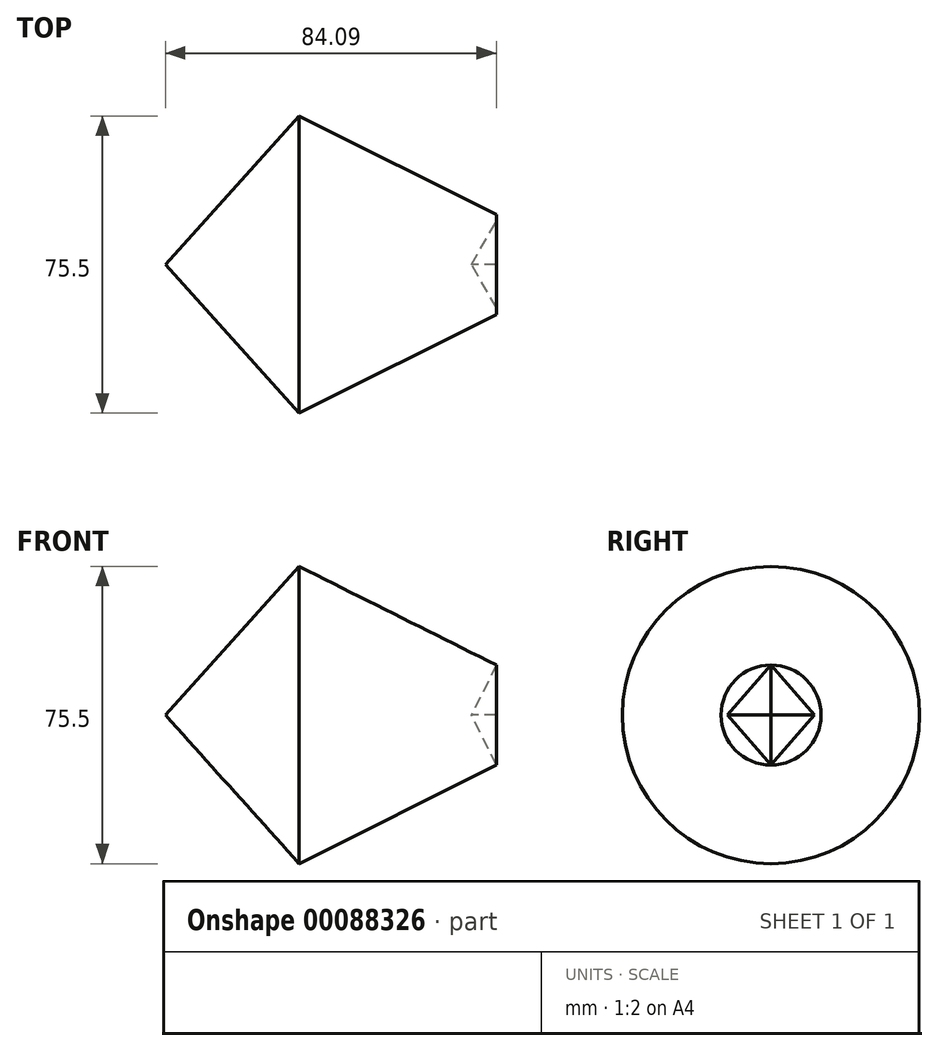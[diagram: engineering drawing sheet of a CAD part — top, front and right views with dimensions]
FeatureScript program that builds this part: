
annotation { "Feature Type Name" : "Feature", "Feature Type Description" : "" }
export const myFeature = defineFeature(function(context is Context, id is Id, definition is map)
    precondition{}
    {
        {
            var Q0;
            Q0=qCreatedBy(makeId("Front.planeOp"),FACE);
            var sketch = newSketch(context, id + "F0", { "sketchPlane" : qUnion([Q0])});
            skPoint(sketch, "E0", {"position": v(-12.7, 0) * mm});
            skPoint(sketch, "E1", {"position": v(12.7, 0) * mm});
            skPoint(sketch, "E2", {"position": v(0, 25.4) * mm});
            skPoint(sketch, "E3", {"position": v(0, -25.4) * mm});
            skLineSegment(sketch, "E4", {"start": v(0, 25.4) * mm, "end": v(-12.7, 0) * mm});
            skLineSegment(sketch, "E5", {"start": v(-12.7, 0) * mm, "end": v(0, -25.4) * mm});
            skLineSegment(sketch, "E6", {"start": v(0, -25.4) * mm, "end": v(12.7, 0) * mm});
            skLineSegment(sketch, "E7", {"start": v(12.7, 0) * mm, "end": v(0, 25.4) * mm});
            skLineSegment(sketch, "E8", {"start": v(0, 25.4) * mm, "end": v(0, 30.48) * mm});
            skLineSegment(sketch, "E9", {"start": v(-56.44, 37.75) * mm, "end": v(-90.44, 0) * mm});
            skLineSegment(sketch, "E10", {"start": v(-90.44, 0) * mm, "end": v(-12.7, 0) * mm});
            skLineSegment(sketch, "E11", {"start": v(-12.7, 0) * mm, "end": v(0, 0) * mm});
            skLineSegment(sketch, "E12", {"start": v(0, 0) * mm, "end": v(0, 25.4) * mm});
            skLineSegment(sketch, "E13", {"start": v(-6.35, 12.7) * mm, "end": v(-56.44, 37.75) * mm});
            skLineSegment(sketch, "E14", {"start": v(-6.35, 12.7) * mm, "end": v(-6.35, 0) * mm});
            skSolve(sketch);
        }
        {
            var Q0;
            Q0=makeQuery(id+"F0.imprint","IMPRINT",FACE,{"disambiguationData":[TD([[makeQuery(id+"F0.imprint","IMPRINT",EDGE,{"derivedFrom":sQuery(id+"F0.wireOp",EDGE,"E4")}),1.0]])]});
            var Q1;
            Q1=makeQuery(id+"F0.imprint","IMPRINT",FACE,{"disambiguationData":[TD([[makeQuery(id+"F0.imprint","IMPRINT",EDGE,{"derivedFrom":sQuery(id+"F0.wireOp",EDGE,"E4")}),-1.0]])]});
            var Q2;
            Q2=sQuery(id+"F0.wireOp",EDGE,"E11");
            revolve(context, id + "F1", {"entities" : qUnion([Q0, Q1]), "axis" : qUnion([Q2]), "revolveType" : RevolveType.FULL});
        }
        {
            var Q0;
            Q0=qCreatedBy(makeId("Top.planeOp"),FACE);
            var sketch = newSketch(context, id + "F2", { "sketchPlane" : qUnion([Q0])});
            skCircle(sketch, "E15.cCircle", {"center": v(0, 0) * mm, "radius": 11 * mm, "construction": true});
            skLineSegment(sketch, "E15.0", {"start": v(6.35, -11) * mm, "end": v(-6.35, -11) * mm});
            skLineSegment(sketch, "E15.1", {"start": v(-6.35, -11) * mm, "end": v(-12.7, 0) * mm});
            skLineSegment(sketch, "E15.2", {"start": v(-12.7, 0) * mm, "end": v(-6.35, 11) * mm});
            skLineSegment(sketch, "E15.3", {"start": v(-6.35, 11) * mm, "end": v(6.35, 11) * mm});
            skLineSegment(sketch, "E15.4", {"start": v(6.35, 11) * mm, "end": v(12.7, 0) * mm});
            skLineSegment(sketch, "E15.5", {"start": v(12.7, 0) * mm, "end": v(6.35, -11) * mm});
            skPoint(sketch, "E15.0.midPoint", {"position": v(0, -11) * mm});
            skSolve(sketch);
        }
        {
            var Q0;
            Q0=qCreatedBy(makeId("Top.planeOp"),FACE);
            cPlane(context, id + "F3", {"entities" : qUnion([Q0]), "cplaneType" : CPlaneType.OFFSET, "offset" : 25.4 * mm, "width" : 152.4 * mm, "height" : 152.4 * mm});
        }
        {
            var Q0;
            Q0=qCreatedBy(makeId("Top.planeOp"),FACE);
            cPlane(context, id + "F4", {"entities" : qUnion([Q0]), "cplaneType" : CPlaneType.OFFSET, "offset" : 25.4 * mm, "oppositeDirection" : true, "width" : 152.4 * mm, "height" : 152.4 * mm});
        }
        {
            var Q0;
            Q0=qCreatedBy(id+"F3.planeOp",FACE);
            var sketch = newSketch(context, id + "F5", { "sketchPlane" : qUnion([Q0])});
            skPoint(sketch, "E16", {"position": v(0, 0) * mm});
            skSolve(sketch);
        }
        {
            var Q0;
            Q0=qCreatedBy(id+"F4.planeOp",FACE);
            var sketch = newSketch(context, id + "F6", { "sketchPlane" : qUnion([Q0])});
            skPoint(sketch, "E17", {"position": v(0, 0) * mm});
            skSolve(sketch);
        }
        {
            var Q1;
            Q1=sQuery(id+"F6.wireOp",VERTEX,"E17");
            var Q2;
            Q2 = qSketchRegion(id + "F2", true);
            loft(context, id + "F7", {"operationType" : NewBodyOperationType.REMOVE, "sheetProfilesArray" : [{ "sheetProfileEntities" : qUnion([Q1]) }, { "sheetProfileEntities" : qUnion([Q2]) }]});
        }
        {
            var Q0;
            Q0=sQuery(id+"F5.wireOp",VERTEX,"E16");
            var Q1;
            Q1 = qSketchRegion(id + "F2", true);
            loft(context, id + "F8", {"operationType" : NewBodyOperationType.REMOVE, "sheetProfilesArray" : [{ "sheetProfileEntities" : qUnion([Q0]) }, { "sheetProfileEntities" : qUnion([Q1]) }]});
        }
    });
